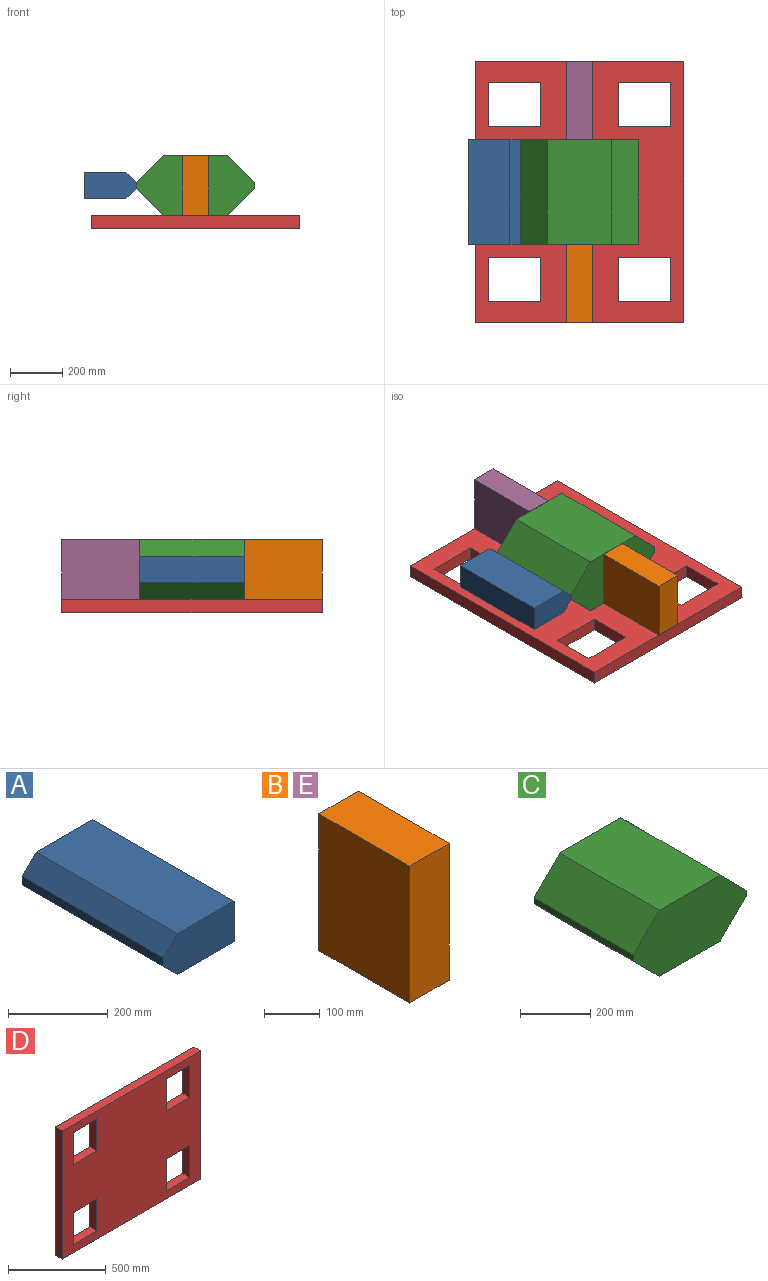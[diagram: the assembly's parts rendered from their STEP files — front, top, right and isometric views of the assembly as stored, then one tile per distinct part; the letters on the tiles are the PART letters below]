
ASSEMBLY  parts=5 mates=5
PART A: 8 faces, bbox 200x400x100 mm
  f0: plane 400x39.73mm, normal (-0.71,0,0.71), area 22410mm2, adj f1,f5,f6,f7
  f1: plane 400x21mm, normal (-1,0,0), area 8400mm2, adj f0,f2,f6,f7
  f2: plane 400x39.73mm, normal (-0.71,0,-0.71), area 22410mm2, adj f1,f3,f6,f7
  f3: plane 400x160.27mm, normal (0,0,-1), area 64107.6mm2, adj f2,f4,f6,f7
  f4: plane 400x100mm, normal (1,0,0), area 40000mm2, adj f3,f5,f6,f7
  f5: plane 400x160.27mm, normal (0,0,1), area 64107.6mm2, adj f0,f4,f6,f7
  f6: plane 200x100mm, normal (0,1,0), area 18430.6mm2, adj f0,f1,f2,f3,f4,f5
  f7: plane 200x100mm, normal (0,-1,0), area 18430.6mm2, adj f0,f1,f2,f3,f4,f5
PART B: 6 faces, bbox 100x230x300 mm
  f0: plane 300x100mm, normal (0,1,0), area 30000mm2, adj f1,f3,f4,f5
  f1: plane 300x230mm, normal (-1,0,0), area 69000mm2, adj f0,f2,f4,f5
  f2: plane 300x100mm, normal (0,-1,0), area 30000mm2, adj f1,f3,f4,f5
  f3: plane 300x230mm, normal (1,0,0), area 69000mm2, adj f0,f2,f4,f5
  f4: plane 230x100mm, normal (0,0,1), area 23000mm2, adj f0,f1,f2,f3
  f5: plane 230x100mm, normal (0,0,-1), area 23000mm2, adj f0,f1,f2,f3
PART C: 10 faces, bbox 454x400x230.1 mm
  f0: plane 400x246mm, normal (0,0,-1), area 98400mm2, adj f1,f7,f8,f9
  f1: plane 400x104.56mm, normal (0.71,0,-0.71), area 58979mm2, adj f0,f2,f8,f9
  f2: plane 400x21mm, normal (1,0,0), area 8400mm2, adj f1,f3,f8,f9
  f3: plane 400x104.52mm, normal (0.71,0,0.71), area 58979mm2, adj f2,f4,f8,f9
  f4: plane 400x246mm, normal (0,0,1), area 98400mm2, adj f3,f5,f8,f9
  f5: plane 400x104.52mm, normal (-0.71,0,0.71), area 58979mm2, adj f4,f6,f8,f9
  f6: plane 400x21mm, normal (-1,0,0), area 8400mm2, adj f5,f7,f8,f9
  f7: plane 400x104.48mm, normal (-0.71,0,-0.71), area 58979mm2, adj f0,f6,f8,f9
  f8: plane 454x230.09mm, normal (0,-1,0), area 82699.1mm2, adj f0,f1,f2,f3,f4,f5,f6,f7
  f9: plane 454x230.09mm, normal (0,1,0), area 82699.1mm2, adj f0,f1,f2,f3,f4,f5,f6,f7
PART D: 22 faces, bbox 1000x50x800 mm
  f0: plane 1000x800mm, normal (0,1,0), area 664000mm2, adj f2,f3,f4,f5,f6,f7,f8,f9
  f1: plane 1000x800mm, normal (0,-1,0), area 664000mm2, adj f2,f3,f4,f5,f6,f7,f8,f9
  f2: plane 800x50mm, normal (1,0,0), area 40000mm2, adj f0,f1,f3,f5
  f3: plane 1000x50mm, normal (0,0,-1), area 50000mm2, adj f0,f1,f2,f4
  f4: plane 800x50mm, normal (-1,0,0), area 40000mm2, adj f0,f1,f3,f5
  f5: plane 1000x50mm, normal (0,0,1), area 50000mm2, adj f0,f1,f2,f4
  f6: plane 170x50mm, normal (0,0,-1), area 8500mm2, adj f0,f1,f7,f8
  f7: plane 200x50mm, normal (-1,0,0), area 10000mm2, adj f0,f1,f6,f9
  f8: plane 200x50mm, normal (1,0,0), area 10000mm2, adj f0,f1,f6,f9
  f9: plane 170x50mm, normal (0,0,1), area 8500mm2, adj f0,f1,f7,f8
  f10: plane 200x50mm, normal (1,0,0), area 10000mm2, adj f0,f1,f11,f12
  f11: plane 170x50mm, normal (0,0,-1), area 8500mm2, adj f0,f1,f10,f13
  f12: plane 170x50mm, normal (0,0,1), area 8500mm2, adj f0,f1,f10,f13
  f13: plane 200x50mm, normal (-1,0,0), area 10000mm2, adj f0,f1,f11,f12
  f14: plane 200x50mm, normal (-1,0,0), area 10000mm2, adj f0,f1,f15,f17
  f15: plane 170x50mm, normal (0,0,-1), area 8500mm2, adj f0,f1,f14,f16
  f16: plane 200x50mm, normal (1,0,0), area 10000mm2, adj f0,f1,f15,f17
  f17: plane 170x50mm, normal (0,0,1), area 8500mm2, adj f0,f1,f14,f16
  f18: plane 200x50mm, normal (-1,0,0), area 10000mm2, adj f0,f1,f19,f21
  f19: plane 170x50mm, normal (0,0,-1), area 8500mm2, adj f0,f1,f18,f20
  f20: plane 200x50mm, normal (1,0,0), area 10000mm2, adj f0,f1,f19,f21
  f21: plane 170x50mm, normal (0,0,1), area 8500mm2, adj f0,f1,f18,f20
PART E: same geometry as B
PLACE A rot(axis=(0,-1,0),180deg) t=(-123,200,0.04)mm
PLACE B rot(axis=(-1,0,0),90deg) t=(-50,-500,0)mm
PLACE C rot(axis=(0,0,-1),180deg) t=(-123,-200,-230.09)mm
PLACE D rot(axis=(-0.58,0.58,-0.58),120deg) t=(-115.11,-123.02,-230.08)mm
PLACE E rot(axis=(0,0.71,-0.71),180deg) t=(50,500,0)mm
MATE fastened A.f1 <-> C.f2  axis (1,0,0) through (-227,0,-115.02)mm
MATE planar E.f4 <-> C.f8  axis (0,-1,0) through (0,200,-115)mm
MATE fastened B.f2 <-> C.f4  axis (0,0,1) through (0,-200,0)mm
MATE fastened E.f2 <-> C.f4  axis (0,0,1) through (0,200,0)mm
MATE fastened C.f0 <-> D.f1  axis (0,0,-1) through (-0.04,0,-230.04)mm
